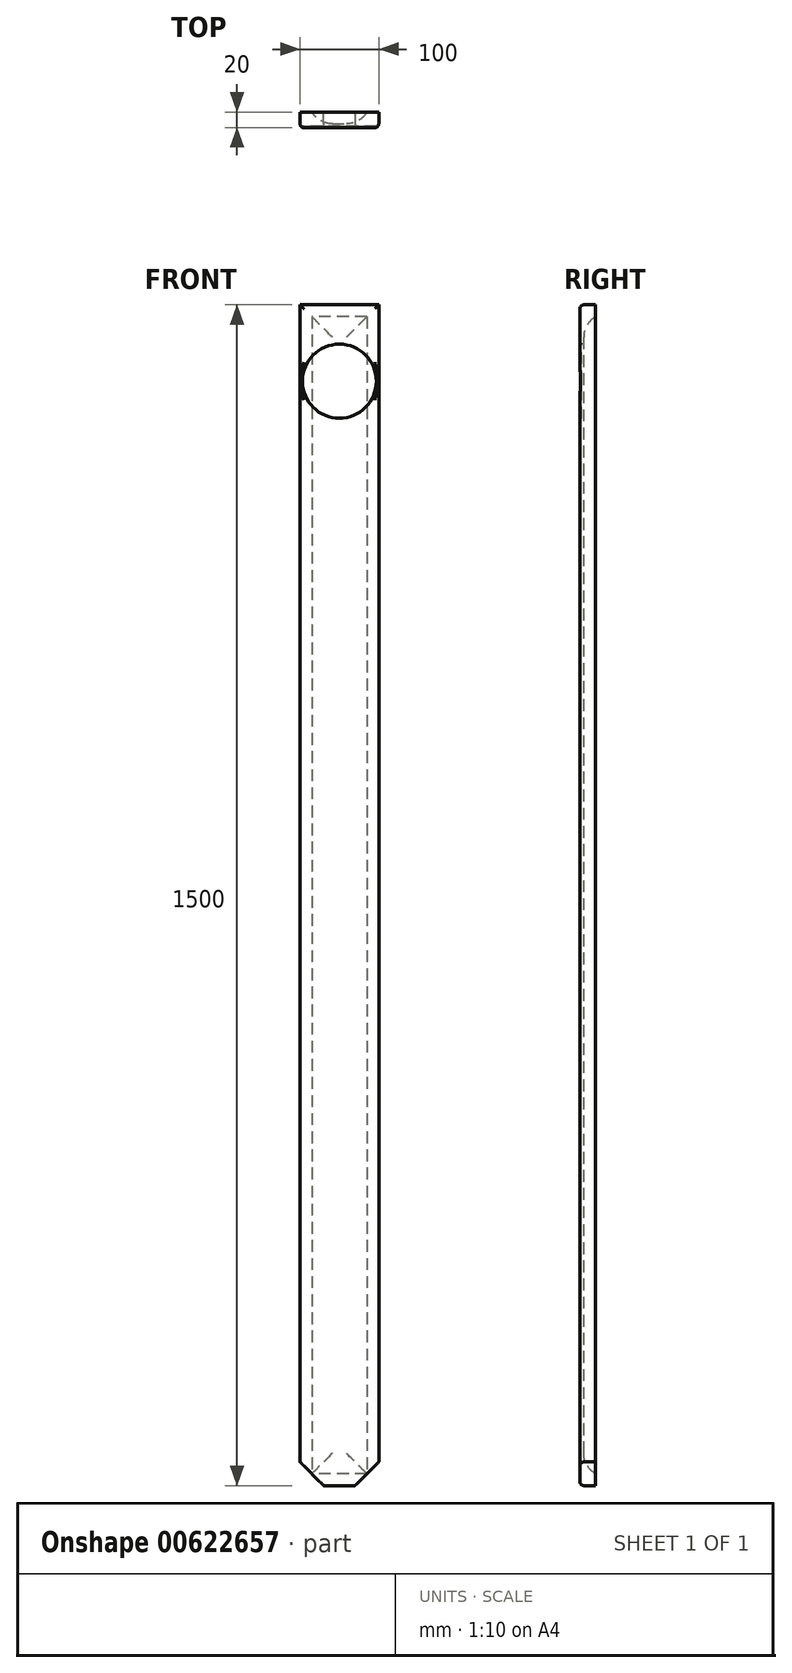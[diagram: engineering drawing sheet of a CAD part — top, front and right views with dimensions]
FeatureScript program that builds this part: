
annotation { "Feature Type Name" : "Feature", "Feature Type Description" : "" }
export const myFeature = defineFeature(function(context is Context, id is Id, definition is map)
    precondition{}
    {
        {
            var Q0;
            Q0=qCreatedBy(makeId("Top.planeOp"),FACE);
            var sketch = newSketch(context, id + "F0", { "sketchPlane" : qUnion([Q0])});
            skLineSegment(sketch, "E0.bottom", {"start": v(50, -10) * mm, "end": v(-50, -10) * mm});
            skLineSegment(sketch, "E0.top", {"start": v(50, 10) * mm, "end": v(-50, 10) * mm});
            skLineSegment(sketch, "E0.left", {"start": v(50, -10) * mm, "end": v(50, 10) * mm});
            skLineSegment(sketch, "E0.right", {"start": v(-50, -10) * mm, "end": v(-50, 10) * mm});
            skPoint(sketch, "E0.middle", {"position": v(0, 0) * mm});
            skSolve(sketch);
        }
        {
            var Q0;
            Q0=makeQuery(id+"F0.imprint","IMPRINT",FACE,{"disambiguationData":[TD([[makeQuery(id+"F0.imprint","IMPRINT",EDGE,{"derivedFrom":sQuery(id+"F0.wireOp",EDGE,"E0.bottom")}),-1.0]])]});
            extrude(context, id + "F1", {"entities" : qUnion([Q0]), "endBound" : BoundingType.SYMMETRIC, "depth" : 1500 * mm, "offsetDistance" : 25 * mm});
        }
        {
            var Q0;
            Q0=makeQuery(id+"F1.opExtrude","SWEPT_FACE",FACE,{"disambiguationData":[OSD([sQuery(id+"F0.wireOp",EDGE,"E0.bottom")])]});
            var sketch = newSketch(context, id + "F2", { "sketchPlane" : qUnion([Q0])});
            skLineSegment(sketch, "E1", {"start": v(0, 750) * mm, "end": v(0, 700) * mm, "construction": true});
            skPoint(sketch, "E1.endSnap0", {"position": v(0, 750) * mm});
            skCircle(sketch, "E2", {"center": v(0, 653) * mm, "radius": 47 * mm});
            skLineSegment(sketch, "E3", {"start": v(-47, 653) * mm, "end": v(-47, 750) * mm, "construction": true});
            skSolve(sketch);
        }
        {
            var Q0;
            Q0=makeQuery(id+"F2.imprint","IMPRINT",FACE,{"disambiguationData":[TD([[makeQuery(id+"F2.imprint","IMPRINT",EDGE,{"derivedFrom":sQuery(id+"F2.wireOp",EDGE,"E2")}),1.0]])]});
            extrude(context, id + "F3", {"entities" : qUnion([Q0]), "operationType" : NewBodyOperationType.REMOVE, "oppositeDirection" : true, "depth" : 2 * mm, "offsetDistance" : 25 * mm});
        }
        {
            var Q0;
            Q0=makeQuery(id+"F1.opExtrude","SWEPT_FACE",FACE,{"disambiguationData":[OSD([sQuery(id+"F0.wireOp",EDGE,"E0.top")])]});
            var sketch = newSketch(context, id + "F4", { "sketchPlane" : qUnion([Q0])});
            skLineSegment(sketch, "E4.0", {"start": v(-35, 735) * mm, "end": v(35, 735) * mm});
            skLineSegment(sketch, "E4.1", {"start": v(-35, 735) * mm, "end": v(-35, -735) * mm});
            skLineSegment(sketch, "E4.2", {"start": v(-35, -735) * mm, "end": v(35, -735) * mm});
            skLineSegment(sketch, "E4.3", {"start": v(35, 735) * mm, "end": v(35, -735) * mm});
            skSolve(sketch);
        }
        {
            var Q0;
            Q0=makeQuery(id+"F4.imprint","IMPRINT",FACE,{"disambiguationData":[TD([[makeQuery(id+"F4.imprint","IMPRINT",EDGE,{"derivedFrom":sQuery(id+"F4.wireOp",EDGE,"E4.0")}),-1.0]])]});
            extrude(context, id + "F5", {"entities" : qUnion([Q0]), "operationType" : NewBodyOperationType.REMOVE, "oppositeDirection" : true, "depth" : 15 * mm, "offsetDistance" : 25 * mm});
        }
        {
            var Q0;
            Q0=makeQuery(id+"F5.boolean.opBoolean","COPY",FACE,{"derivedFrom":makeQuery(id+"F5.opExtrude","CAP_FACE",FACE,{"disambiguationData":[OSD([sQuery(id+"F4.wireOp",EDGE,"E4.0"),sQuery(id+"F4.wireOp",EDGE,"E4.1"),sQuery(id+"F4.wireOp",EDGE,"E4.2"),sQuery(id+"F4.wireOp",EDGE,"E4.3")])],"isStart":false})});
            fillet(context, id + "F6", {"entities" : qUnion([Q0]), "radius" : 30 * mm, "tangentPropagation" : true, "allowEdgeOverflow" : false});
        }
        {
            var Q0;
            Q0=makeQuery(id+"F1.opExtrude","SWEPT_FACE",FACE,{"disambiguationData":[OSD([sQuery(id+"F0.wireOp",EDGE,"E0.bottom")])]});
            fillet(context, id + "F7", {"entities" : qUnion([Q0]), "radius" : 5 * mm, "tangentPropagation" : true, "allowEdgeOverflow" : false});
        }
        {
            var Q0;
            Q0=makeQuery(id+"F1.opExtrude","CAP_EDGE",EDGE,{"disambiguationData":[OSD([sQuery(id+"F0.wireOp",EDGE,"E0.left")])],"isStart":true});
            var Q1;
            Q1=makeQuery(id+"F1.opExtrude","CAP_EDGE",EDGE,{"disambiguationData":[OSD([sQuery(id+"F0.wireOp",EDGE,"E0.right")])],"isStart":true});
            chamfer(context, id + "F8", {"entities" : qUnion([Q0, Q1]), "width" : 30 * mm});
        }
    });
